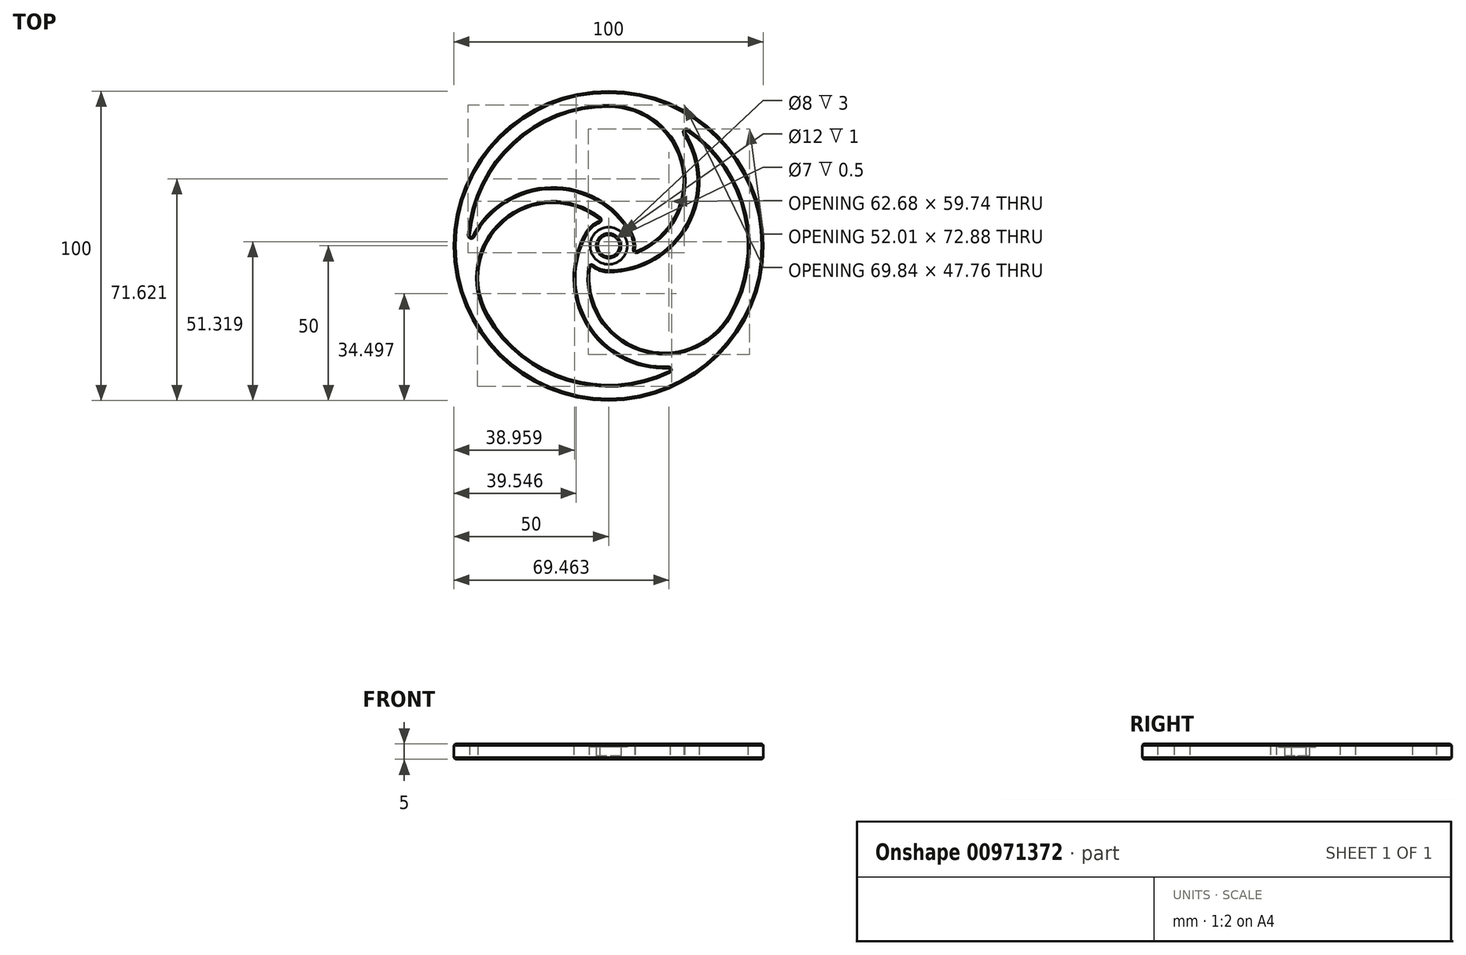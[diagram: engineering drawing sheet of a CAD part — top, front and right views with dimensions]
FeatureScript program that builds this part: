
annotation { "Feature Type Name" : "Feature", "Feature Type Description" : "" }
export const myFeature = defineFeature(function(context is Context, id is Id, definition is map)
    precondition{}
    {
        {
            var Q0;
            Q0=qCreatedBy(makeId("Top.planeOp"),FACE);
            var sketch = newSketch(context, id + "F0", { "sketchPlane" : qUnion([Q0])});
            skCircle(sketch, "E0", {"center": v(0, 0) * mm, "radius": 4 * mm});
            skCircle(sketch, "E1", {"center": v(0, 0) * mm, "radius": 7.5 * mm, "construction": true});
            skCircle(sketch, "E2.cCircle", {"center": v(0, 0) * mm, "radius": 50 * mm});
            skArc(sketch, "E3", {"start": v(0, 45) * mm, "mid": v(-31.53, 32.1) * mm, "end": v(-45, 0.82) * mm});
            skArc(sketch, "E4.cCircle", {"start": v(0, 45) * mm, "mid": v(-31.53, 32.1) * mm, "end": v(-45, 0.82) * mm, "construction": true});
            skLineSegment(sketch, "E4.0", {"start": v(0, 45) * mm, "end": v(38.97, -22.5) * mm, "construction": true});
            skLineSegment(sketch, "E4.1", {"start": v(38.97, -22.5) * mm, "end": v(-38.97, -22.5) * mm, "construction": true});
            skLineSegment(sketch, "E4.2", {"start": v(-38.97, -22.5) * mm, "end": v(0, 45) * mm, "construction": true});
            skPoint(sketch, "E5", {"position": v(0, 8.5) * mm});
            skArc(sketch, "E6.cCircle", {"start": v(-5.9, -6.12) * mm, "mid": v(-3.18, -7.88) * mm, "end": v(0, -8.5) * mm});
            skCircle(sketch, "E7", {"center": v(0, 0) * mm, "radius": 3.5 * mm, "construction": true});
            skPoint(sketch, "E8", {"position": v(0, -8.5) * mm});
            skPoint(sketch, "E9", {"position": v(0, 50) * mm});
            skLineSegment(sketch, "E10", {"start": v(0, 50) * mm, "end": v(0, -8.5) * mm, "construction": true});
            skArc(sketch, "E11.trimOffspring", {"start": v(0, -8.5) * mm, "mid": v(26.23, 7.81) * mm, "end": v(23.2, 38.55) * mm});
            skArc(sketch, "E12.trimOffspring", {"start": v(8.25, -2.05) * mm, "mid": v(23.89, 24.94) * mm, "end": v(0, 45) * mm});
            skArc(sketch, "E13.1.0", {"start": v(-2.35, 8.17) * mm, "mid": v(-33.54, 8.22) * mm, "end": v(-38.97, -22.5) * mm});
            skArc(sketch, "E13.1.1", {"start": v(7.36, 4.25) * mm, "mid": v(-19.88, 18.81) * mm, "end": v(-45, 0.82) * mm});
            skArc(sketch, "E13.2.0", {"start": v(-5.9, -6.12) * mm, "mid": v(9.65, -33.15) * mm, "end": v(38.97, -22.5) * mm});
            skArc(sketch, "E13.2.1", {"start": v(-7.36, 4.25) * mm, "mid": v(-6.35, -26.62) * mm, "end": v(21.79, -39.38) * mm});
            skArc(sketch, "E14.trimOffspring", {"start": v(0, 8.5) * mm, "mid": v(-4.25, 7.36) * mm, "end": v(-7.36, 4.25) * mm});
            skArc(sketch, "E15.trimOffspring", {"start": v(8.25, -2.05) * mm, "mid": v(8.42, 1.18) * mm, "end": v(7.36, 4.25) * mm});
            skArc(sketch, "E16.trimOffspring", {"start": v(38.97, -22.5) * mm, "mid": v(43.57, 11.25) * mm, "end": v(23.2, 38.55) * mm, "construction": true});
            skArc(sketch, "E17.trimOffspring", {"start": v(38.97, -22.5) * mm, "mid": v(43.57, 11.25) * mm, "end": v(23.2, 38.55) * mm});
            skArc(sketch, "E18.trimOffspring", {"start": v(-38.97, -22.5) * mm, "mid": v(-12.04, -43.36) * mm, "end": v(21.79, -39.38) * mm, "construction": true});
            skArc(sketch, "E19.trimOffspring", {"start": v(-38.97, -22.5) * mm, "mid": v(-12.04, -43.36) * mm, "end": v(21.79, -39.38) * mm});
            skCircle(sketch, "E20", {"center": v(0, 0) * mm, "radius": 6 * mm});
            skSolve(sketch);
        }
        {
            var Q0;
            Q0=makeQuery(id+"F0.imprint","IMPRINT",FACE,{"disambiguationData":[TD([[makeQuery(id+"F0.imprint","IMPRINT",EDGE,{"derivedFrom":sQuery(id+"F0.wireOp",EDGE,"E0")}),-1.0]])]});
            var Q1;
            Q1=makeQuery(id+"F0.imprint","IMPRINT",FACE,{"disambiguationData":[TD([[makeQuery(id+"F0.imprint","IMPRINT",EDGE,{"derivedFrom":sQuery(id+"F0.wireOp",EDGE,"E2.cCircle")}),1.0]])]});
            extrude(context, id + "F1", {"entities" : qUnion([Q0, Q1]), "depth" : 5 * mm, "offsetDistance" : 25 * mm});
        }
        {
            var Q0;
            Q0=makeQuery(id+"F1.opExtrude","SWEPT_EDGE",EDGE,{"disambiguationData":[OSD([sQuery(id+"F0.wireOp",EDGE,"E11.trimOffspring"),sQuery(id+"F0.wireOp",EDGE,"E17.trimOffspring")])]});
            var Q1;
            Q1=makeQuery(id+"F1.opExtrude","SWEPT_EDGE",EDGE,{"disambiguationData":[OSD([sQuery(id+"F0.wireOp",EDGE,"E13.2.1"),sQuery(id+"F0.wireOp",EDGE,"E19.trimOffspring")])]});
            var Q2;
            Q2=makeQuery(id+"F1.opExtrude","SWEPT_EDGE",EDGE,{"disambiguationData":[OSD([sQuery(id+"F0.wireOp",EDGE,"E3"),sQuery(id+"F0.wireOp",EDGE,"E13.1.1")])]});
            var Q3;
            Q3=makeQuery(id+"F1.opExtrude","SWEPT_EDGE",EDGE,{"disambiguationData":[OSD([sQuery(id+"F0.wireOp",EDGE,"E6.cCircle"),sQuery(id+"F0.wireOp",EDGE,"E13.2.0")])]});
            var Q4;
            Q4=makeQuery(id+"F1.opExtrude","SWEPT_EDGE",EDGE,{"disambiguationData":[OSD([sQuery(id+"F0.wireOp",EDGE,"E12.trimOffspring"),sQuery(id+"F0.wireOp",EDGE,"E15.trimOffspring")])]});
            var Q5;
            Q5=makeQuery(id+"F1.opExtrude","SWEPT_EDGE",EDGE,{"disambiguationData":[OSD([sQuery(id+"F0.wireOp",EDGE,"E13.1.0"),sQuery(id+"F0.wireOp",EDGE,"E14.trimOffspring")])]});
            fillet(context, id + "F2", {"entities" : qUnion([Q0, Q1, Q2, Q3, Q4, Q5]), "radius" : .5 * mm, "tangentPropagation" : true, "allowEdgeOverflow" : false});
        }
        {
            var Q0;
            Q0=makeQuery(id+"F0.imprint","IMPRINT",FACE,{"disambiguationData":[TD([[makeQuery(id+"F0.imprint","IMPRINT",EDGE,{"derivedFrom":sQuery(id+"F0.wireOp",EDGE,"E0")}),-1.0]])]});
            extrude(context, id + "F3", {"entities" : qUnion([Q0]), "operationType" : NewBodyOperationType.REMOVE, "depth" : 5 * mm, "offsetDistance" : 25 * mm, "hasSecondDirection" : true, "secondDirectionOppositeDirection" : false, "secondDirectionDepth" : 4 * mm});
        }
        {
            var Q0;
            Q0=qCreatedBy(makeId("Top.planeOp"),FACE);
            var sketch = newSketch(context, id + "F4", { "sketchPlane" : qUnion([Q0])});
            skCircle(sketch, "E21", {"center": v(0, 0) * mm, "radius": 4 * mm});
            skCircle(sketch, "E22", {"center": v(0, 0) * mm, "radius": 3.5 * mm});
            skSolve(sketch);
        }
        {
            var Q0;
            Q0 = qSketchRegion(id + "F4", true);
            extrude(context, id + "F5", {"entities" : qUnion([Q0]), "depth" : 1 * mm, "offsetDistance" : 25 * mm});
        }
        {
            var Q0;
            Q0=makeQuery(id+"F1.opExtrude","SWEPT_BODY",BODY,{"disambiguationData":[OSD([sQuery(id+"F0.wireOp",EDGE,"E0"),sQuery(id+"F0.wireOp",EDGE,"E2.cCircle"),sQuery(id+"F0.wireOp",EDGE,"E3"),sQuery(id+"F0.wireOp",EDGE,"E6.cCircle"),sQuery(id+"F0.wireOp",EDGE,"E11.trimOffspring"),sQuery(id+"F0.wireOp",EDGE,"E12.trimOffspring"),sQuery(id+"F0.wireOp",EDGE,"E13.1.0"),sQuery(id+"F0.wireOp",EDGE,"E13.1.1"),sQuery(id+"F0.wireOp",EDGE,"E13.2.0"),sQuery(id+"F0.wireOp",EDGE,"E13.2.1"),sQuery(id+"F0.wireOp",EDGE,"E14.trimOffspring"),sQuery(id+"F0.wireOp",EDGE,"E15.trimOffspring"),sQuery(id+"F0.wireOp",EDGE,"E17.trimOffspring"),sQuery(id+"F0.wireOp",EDGE,"E19.trimOffspring")])]});
            var Q1;
            Q1=makeQuery(id+"F5.opExtrude","SWEPT_BODY",BODY,{"disambiguationData":[OSD([sQuery(id+"F4.wireOp",EDGE,"E21"),sQuery(id+"F4.wireOp",EDGE,"E22")])]});
            booleanBodies(context, id + "F6", {"operationType" : BooleanOperationType.UNION, "tools" : qUnion([Q0, Q1])});
        }
        {
            var Q0;
            Q0=makeQuery(id+"F6.opBoolean","MERGE",FACE,{"derivedFrom":[makeQuery(id+"F1.opExtrude","CAP_FACE",FACE,{"disambiguationData":[OSD([sQuery(id+"F0.wireOp",EDGE,"E0"),sQuery(id+"F0.wireOp",EDGE,"E2.cCircle"),sQuery(id+"F0.wireOp",EDGE,"E3"),sQuery(id+"F0.wireOp",EDGE,"E6.cCircle"),sQuery(id+"F0.wireOp",EDGE,"E11.trimOffspring"),sQuery(id+"F0.wireOp",EDGE,"E12.trimOffspring"),sQuery(id+"F0.wireOp",EDGE,"E13.1.0"),sQuery(id+"F0.wireOp",EDGE,"E13.1.1"),sQuery(id+"F0.wireOp",EDGE,"E13.2.0"),sQuery(id+"F0.wireOp",EDGE,"E13.2.1"),sQuery(id+"F0.wireOp",EDGE,"E14.trimOffspring"),sQuery(id+"F0.wireOp",EDGE,"E15.trimOffspring"),sQuery(id+"F0.wireOp",EDGE,"E17.trimOffspring"),sQuery(id+"F0.wireOp",EDGE,"E19.trimOffspring")])],"isStart":true}),makeQuery(id+"F5.opExtrude","CAP_FACE",FACE,{"disambiguationData":[OSD([sQuery(id+"F4.wireOp",EDGE,"E21"),sQuery(id+"F4.wireOp",EDGE,"E22")])],"isStart":true})]});
            var Q1;
            Q1=makeQuery(id+"F3.boolean.opBoolean","COPY",EDGE,{"derivedFrom":makeQuery(id+"F3.opExtrude","CAP_EDGE",EDGE,{"disambiguationData":[OSD([sQuery(id+"F0.wireOp",EDGE,"E0")])],"isStart":true})});
            var Q2;
            Q2=makeQuery(id+"F1.opExtrude","CAP_EDGE",EDGE,{"disambiguationData":[OSD([sQuery(id+"F0.wireOp",EDGE,"E13.1.0")])],"isStart":false});
            var Q3;
            Q3=makeQuery(id+"F1.opExtrude","CAP_EDGE",EDGE,{"disambiguationData":[OSD([sQuery(id+"F0.wireOp",EDGE,"E13.1.1")])],"isStart":false});
            var Q4;
            Q4=makeQuery(id+"F1.opExtrude","CAP_EDGE",EDGE,{"disambiguationData":[OSD([sQuery(id+"F0.wireOp",EDGE,"E12.trimOffspring")])],"isStart":false});
            var Q5;
            Q5=makeQuery(id+"F1.opExtrude","CAP_EDGE",EDGE,{"disambiguationData":[OSD([sQuery(id+"F0.wireOp",EDGE,"E11.trimOffspring")])],"isStart":false});
            var Q6;
            Q6=makeQuery(id+"F1.opExtrude","CAP_EDGE",EDGE,{"disambiguationData":[OSD([sQuery(id+"F0.wireOp",EDGE,"E2.cCircle")])],"isStart":false});
            chamfer(context, id + "F7", {"entities" : qUnion([Q0, Q1, Q2, Q3, Q4, Q5, Q6]), "width" : .5 * mm, "tangentPropagation" : true});
        }
    });
